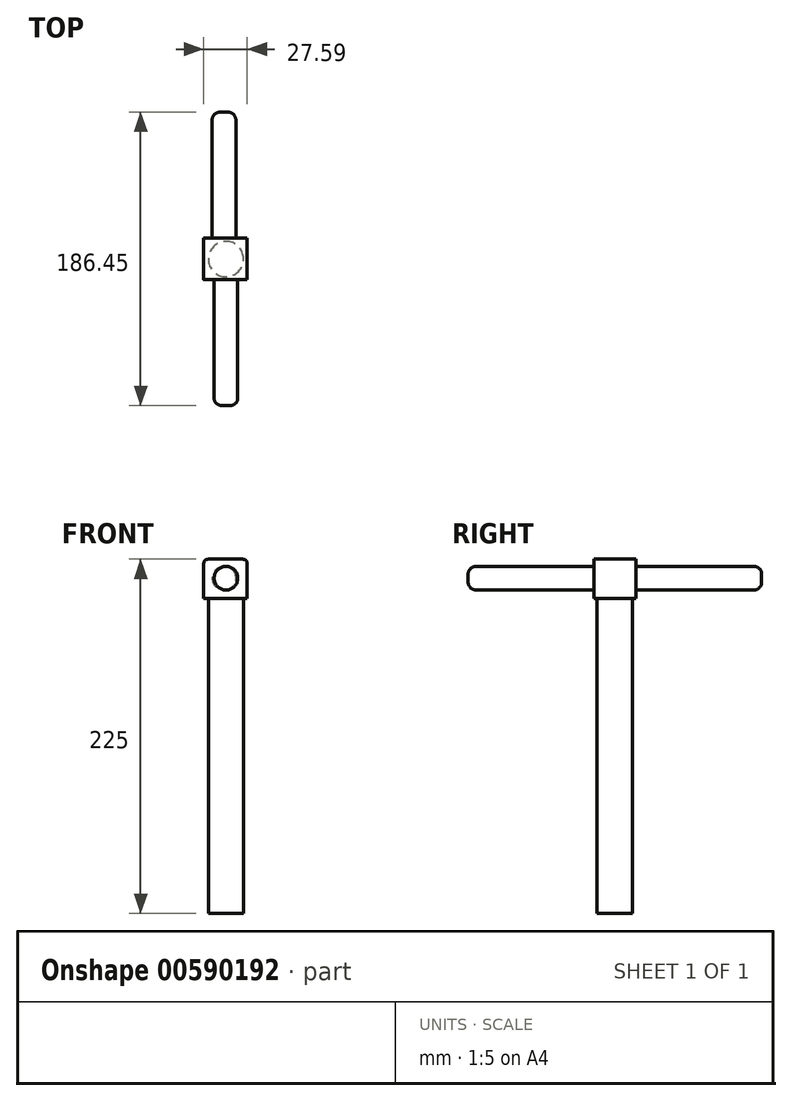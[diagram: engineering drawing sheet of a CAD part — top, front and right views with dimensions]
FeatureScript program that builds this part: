
annotation { "Feature Type Name" : "Feature", "Feature Type Description" : "" }
export const myFeature = defineFeature(function(context is Context, id is Id, definition is map)
    precondition{}
    {
        {
            var Q0;
            Q0=qCreatedBy(makeId("Top.planeOp"),FACE);
            var sketch = newSketch(context, id + "F0", { "sketchPlane" : qUnion([Q0])});
            skCircle(sketch, "E0", {"center": v(0, 0) * mm, "radius": 21.28 * mm});
            skCircle(sketch, "E1", {"center": v(0, 0) * mm, "radius": 11.2 * mm});
            skSolve(sketch);
        }
        {
            var Q0;
            Q0=makeQuery(id+"F0.imprint","IMPRINT",FACE,{"disambiguationData":[TD([[makeQuery(id+"F0.imprint","IMPRINT",EDGE,{"derivedFrom":sQuery(id+"F0.wireOp",EDGE,"OBKUFHPn-Nvc8-66Ed-7zAv-iwnkNmgZCTDl")}),1.0]])]});
            var Q1;
            Q1=makeQuery(id+"F0.imprint","IMPRINT",FACE,{"disambiguationData":[TD([[makeQuery(id+"F0.imprint","IMPRINT",EDGE,{"derivedFrom":sQuery(id+"F0.wireOp",EDGE,"E1")}),1.0]])]});
            extrude(context, id + "F1", {"entities" : qUnion([Q0, Q1]), "depth" : 200 * mm, "offsetDistance" : 25 * mm});
        }
        {
            var Q0;
            Q0=makeQuery(id+"F1.opExtrude","CAP_FACE",FACE,{"disambiguationData":[OSD([sQuery(id+"F0.wireOp",EDGE,"E1")])],"isStart":false});
            var sketch = newSketch(context, id + "F2", { "sketchPlane" : qUnion([Q0])});
            skLineSegment(sketch, "E2.bottom", {"start": v(-14.08, 13.32) * mm, "end": v(13.5, 13.32) * mm});
            skLineSegment(sketch, "E2.top", {"start": v(-14.08, -13.13) * mm, "end": v(13.5, -13.13) * mm});
            skLineSegment(sketch, "E2.left", {"start": v(-14.08, 13.32) * mm, "end": v(-14.08, -13.13) * mm});
            skLineSegment(sketch, "E2.right", {"start": v(13.5, 13.32) * mm, "end": v(13.5, -13.13) * mm});
            skSolve(sketch);
        }
        {
            var Q0;
            Q0 = qSketchRegion(id + "F2", true);
            extrude(context, id + "F3", {"entities" : qUnion([Q0]), "operationType" : NewBodyOperationType.ADD, "depth" : 25 * mm, "offsetDistance" : 25 * mm});
        }
        {
            var Q0;
            Q0=makeQuery(id+"F3.opExtrude","SWEPT_FACE",FACE,{"disambiguationData":[OSD([sQuery(id+"F2.wireOp",EDGE,"E2.top")])]});
            var sketch = newSketch(context, id + "F4", { "sketchPlane" : qUnion([Q0])});
            skCircle(sketch, "E3", {"center": v(0, 212.95) * mm, "radius": 7.51 * mm});
            skSolve(sketch);
        }
        {
            var Q0;
            Q0=makeQuery(id+"F3.opExtrude","SWEPT_FACE",FACE,{"disambiguationData":[OSD([sQuery(id+"F2.wireOp",EDGE,"E2.bottom")])]});
            var sketch = newSketch(context, id + "F5", { "sketchPlane" : qUnion([Q0])});
            skCircle(sketch, "E4", {"center": v(1.22, 212.92) * mm, "radius": 7.56 * mm});
            skSolve(sketch);
        }
        {
            var Q0;
            Q0=makeQuery(id+"F5.imprint","IMPRINT",FACE,{"disambiguationData":[TD([[makeQuery(id+"F5.imprint","IMPRINT",EDGE,{"derivedFrom":sQuery(id+"F5.wireOp",EDGE,"E4")}),1.0]])]});
            extrude(context, id + "F6", {"entities" : qUnion([Q0]), "operationType" : NewBodyOperationType.ADD, "depth" : 80 * mm, "offsetDistance" : 25 * mm});
        }
        {
            var Q0;
            Q0 = qSketchRegion(id + "F4", true);
            extrude(context, id + "F7", {"entities" : qUnion([Q0]), "operationType" : NewBodyOperationType.ADD, "depth" : 80 * mm, "offsetDistance" : 25 * mm});
        }
        {
            var Q0;
            Q0=makeQuery(id+"F3.opExtrude","CAP_EDGE",EDGE,{"disambiguationData":[OSD([sQuery(id+"F2.wireOp",EDGE,"E2.right")])],"isStart":false});
            var Q1;
            Q1=makeQuery(id+"F3.opExtrude","CAP_EDGE",EDGE,{"disambiguationData":[OSD([sQuery(id+"F2.wireOp",EDGE,"E2.left")])],"isStart":false});
            fillet(context, id + "F8", {"entities" : qUnion([Q0, Q1]), "radius" : 3 * mm, "tangentPropagation" : true, "rho" : 0.5, "crossSection" : FilletCrossSection.CONIC, "allowEdgeOverflow" : false});
        }
        {
            var Q0;
            Q0=makeQuery(id+"F6.opExtrude","CAP_EDGE",EDGE,{"disambiguationData":[OSD([sQuery(id+"F5.wireOp",EDGE,"E4")])],"isStart":false});
            fillet(context, id + "F9", {"entities" : qUnion([Q0]), "radius" : 5 * mm, "tangentPropagation" : true, "allowEdgeOverflow" : false});
        }
        {
            var Q0;
            Q0=makeQuery(id+"F7.opExtrude","CAP_EDGE",EDGE,{"disambiguationData":[OSD([sQuery(id+"F4.wireOp",EDGE,"E3")])],"isStart":false});
            fillet(context, id + "F10", {"entities" : qUnion([Q0]), "radius" : 5 * mm, "tangentPropagation" : true, "allowEdgeOverflow" : false});
        }
    });
